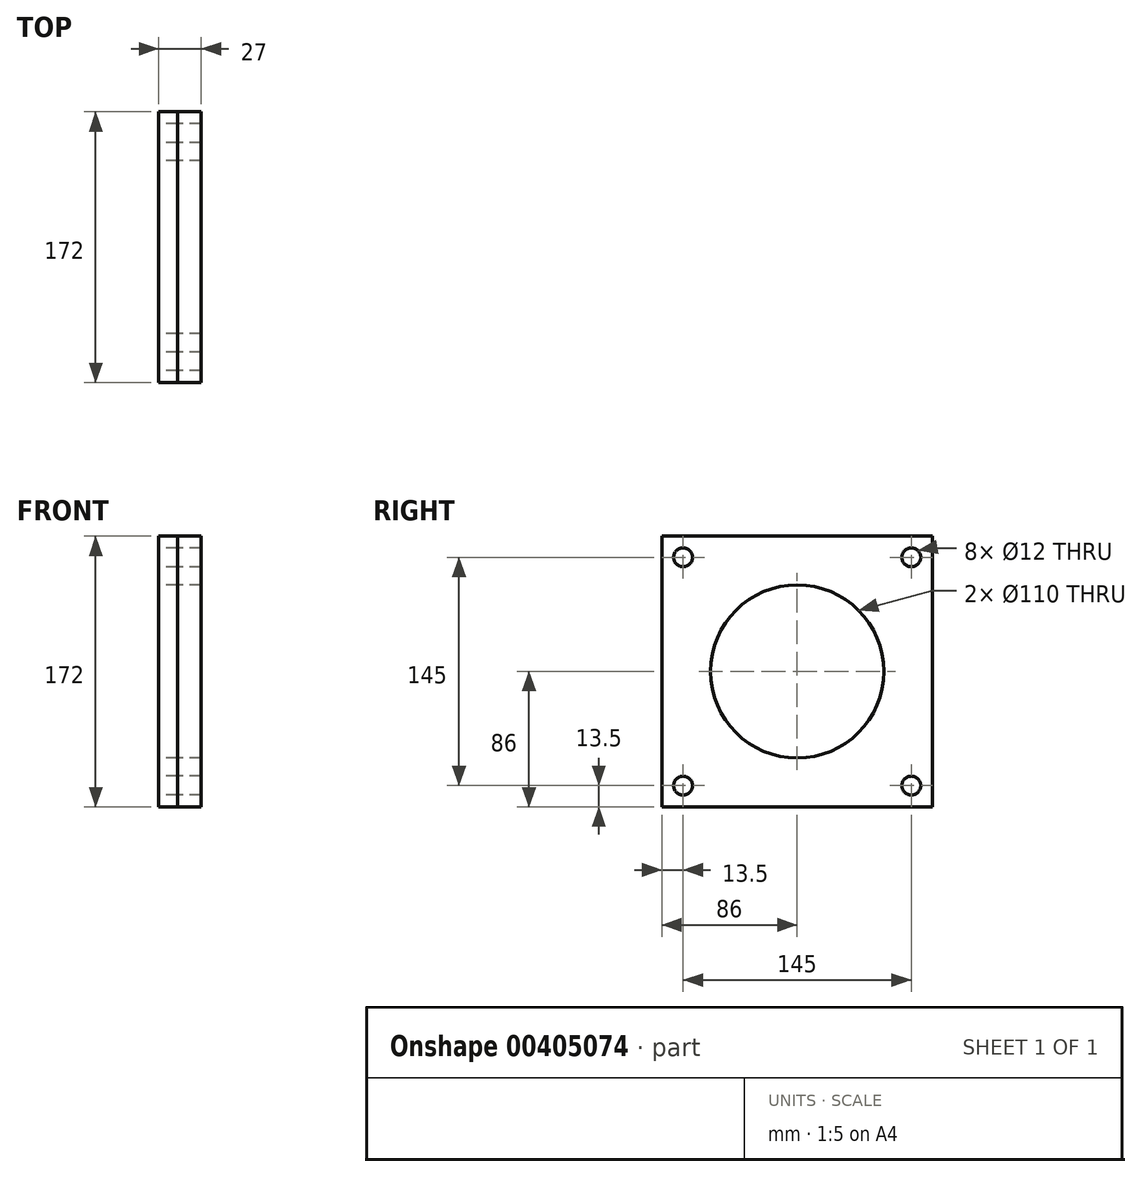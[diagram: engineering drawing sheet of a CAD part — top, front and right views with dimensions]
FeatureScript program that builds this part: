
annotation { "Feature Type Name" : "Feature", "Feature Type Description" : "" }
export const myFeature = defineFeature(function(context is Context, id is Id, definition is map)
    precondition{}
    {
        {
            var Q0;
            Q0=qCreatedBy(makeId("Right.planeOp"),FACE);
            var sketch = newSketch(context, id + "F0", { "sketchPlane" : qUnion([Q0])});
            skLineSegment(sketch, "E0.bottom", {"start": v(-86, 86) * mm, "end": v(86, 86) * mm});
            skLineSegment(sketch, "E0.top", {"start": v(-86, -86) * mm, "end": v(86, -86) * mm});
            skLineSegment(sketch, "E0.left", {"start": v(-86, 86) * mm, "end": v(-86, -86) * mm});
            skLineSegment(sketch, "E0.right", {"start": v(86, 86) * mm, "end": v(86, -86) * mm});
            skSolve(sketch);
        }
        {
            var Q0;
            Q0=makeQuery(id+"F0.imprint","IMPRINT",FACE,{"disambiguationData":[TD([[makeQuery(id+"F0.imprint","IMPRINT",EDGE,{"derivedFrom":sQuery(id+"F0.wireOp",EDGE,"E0.bottom")}),-1.0]])]});
            extrude(context, id + "F1", {"entities" : qUnion([Q0]), "depth" : 15 * mm});
        }
        {
            var Q0;
            Q0 = qSketchRegion(id + "F0", true);
            extrude(context, id + "F2", {"entities" : qUnion([Q0]), "depth" : -12 * mm});
        }
        {
            var Q0;
            Q0=qCreatedBy(makeId("Right.planeOp"),FACE);
            var sketch = newSketch(context, id + "F3", { "sketchPlane" : qUnion([Q0])});
            skCircle(sketch, "E1", {"center": v(-72.5, 72.5) * mm, "radius": 6 * mm});
            skCircle(sketch, "E2.0.1.0", {"center": v(-72.5, -72.5) * mm, "radius": 6 * mm});
            skCircle(sketch, "E2.1.0.0", {"center": v(72.5, 72.5) * mm, "radius": 6 * mm});
            skCircle(sketch, "E2.1.1.0", {"center": v(72.5, -72.5) * mm, "radius": 6 * mm});
            skLineSegment(sketch, "E2.direction1", {"start": v(-72.5, 72.5) * mm, "end": v(72.5, 72.5) * mm, "construction": true});
            skLineSegment(sketch, "E2.direction2", {"start": v(-72.5, 72.5) * mm, "end": v(-72.5, -72.5) * mm, "construction": true});
            skSolve(sketch);
        }
        {
            var Q0;
            Q0 = qSketchRegion(id + "F3", true);
            extrude(context, id + "F4", {"entities" : qUnion([Q0]), "depth" : 25 * mm, "hasSecondDirection" : true, "secondDirectionOppositeDirection" : true, "secondDirectionDepth" : 25 * mm});
        }
        {
            var Q0;
            Q0=makeQuery(id+"F4.opExtrude","SWEPT_BODY",BODY,{"disambiguationData":[OSD([sQuery(id+"F3.wireOp",EDGE,"E1")])]});
            var Q1;
            Q1=makeQuery(id+"F4.opExtrude","SWEPT_BODY",BODY,{"disambiguationData":[OSD([sQuery(id+"F3.wireOp",EDGE,"E2.0.1.0")])]});
            var Q2;
            Q2=makeQuery(id+"F4.opExtrude","SWEPT_BODY",BODY,{"disambiguationData":[OSD([sQuery(id+"F3.wireOp",EDGE,"E2.1.1.0")])]});
            var Q3;
            Q3=makeQuery(id+"F4.opExtrude","SWEPT_BODY",BODY,{"disambiguationData":[OSD([sQuery(id+"F3.wireOp",EDGE,"E2.1.0.0")])]});
            var Q4;
            Q4=makeQuery(id+"F1.opExtrude","SWEPT_BODY",BODY,{"disambiguationData":[OSD([sQuery(id+"F0.wireOp",EDGE,"E0.bottom"),sQuery(id+"F0.wireOp",EDGE,"E0.top"),sQuery(id+"F0.wireOp",EDGE,"E0.left"),sQuery(id+"F0.wireOp",EDGE,"E0.right")])]});
            var Q5;
            Q5=makeQuery(id+"F2.opExtrude","SWEPT_BODY",BODY,{"disambiguationData":[OSD([sQuery(id+"F0.wireOp",EDGE,"E0.bottom"),sQuery(id+"F0.wireOp",EDGE,"E0.top"),sQuery(id+"F0.wireOp",EDGE,"E0.left"),sQuery(id+"F0.wireOp",EDGE,"E0.right")])]});
            booleanBodies(context, id + "F5", {"operationType" : BooleanOperationType.SUBTRACTION, "tools" : qUnion([Q0, Q1, Q2, Q3]), "targets" : qUnion([Q4, Q5])});
        }
        {
            var Q0;
            Q0=qCreatedBy(makeId("Right.planeOp"),FACE);
            var sketch = newSketch(context, id + "F6", { "sketchPlane" : qUnion([Q0])});
            skCircle(sketch, "E3", {"center": v(0, 0) * mm, "radius": 55 * mm});
            skSolve(sketch);
        }
        {
            var Q0;
            Q0=makeQuery(id+"F6.imprint","IMPRINT",FACE,{"disambiguationData":[TD([[makeQuery(id+"F6.imprint","IMPRINT",EDGE,{"derivedFrom":sQuery(id+"F6.wireOp",EDGE,"E3")}),1.0]])]});
            extrude(context, id + "F7", {"entities" : qUnion([Q0]), "depth" : 25 * mm, "hasSecondDirection" : true, "secondDirectionOppositeDirection" : true, "secondDirectionDepth" : 25 * mm});
        }
        {
            var Q0;
            Q0=makeQuery(id+"F7.opExtrude","SWEPT_BODY",BODY,{"disambiguationData":[OSD([sQuery(id+"F6.wireOp",EDGE,"E3")])]});
            var Q1;
            Q1=makeQuery(id+"F1.opExtrude","SWEPT_BODY",BODY,{"disambiguationData":[OSD([sQuery(id+"F0.wireOp",EDGE,"E0.bottom"),sQuery(id+"F0.wireOp",EDGE,"E0.top"),sQuery(id+"F0.wireOp",EDGE,"E0.left"),sQuery(id+"F0.wireOp",EDGE,"E0.right")])]});
            var Q2;
            Q2=makeQuery(id+"F2.opExtrude","SWEPT_BODY",BODY,{"disambiguationData":[OSD([sQuery(id+"F0.wireOp",EDGE,"E0.bottom"),sQuery(id+"F0.wireOp",EDGE,"E0.top"),sQuery(id+"F0.wireOp",EDGE,"E0.left"),sQuery(id+"F0.wireOp",EDGE,"E0.right")])]});
            booleanBodies(context, id + "F8", {"operationType" : BooleanOperationType.SUBTRACTION, "tools" : qUnion([Q0]), "targets" : qUnion([Q1, Q2])});
        }
    });
